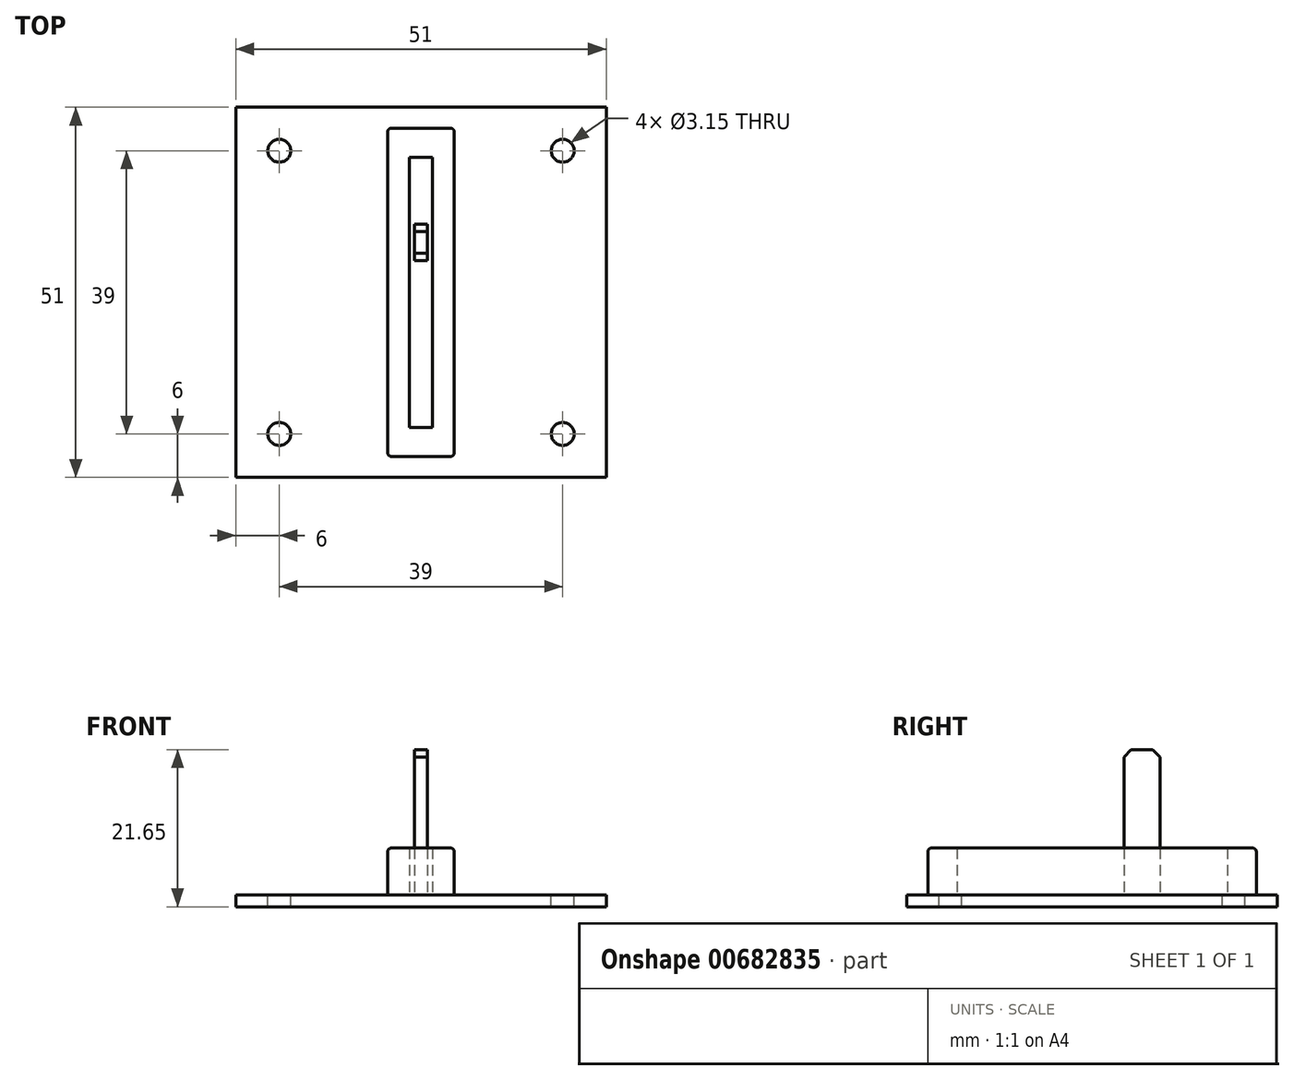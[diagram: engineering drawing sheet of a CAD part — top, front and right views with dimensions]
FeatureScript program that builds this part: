
annotation { "Feature Type Name" : "Feature", "Feature Type Description" : "" }
export const myFeature = defineFeature(function(context is Context, id is Id, definition is map)
    precondition{}
    {
        {
            var Q0;
            Q0=qCreatedBy(makeId("Top.planeOp"),FACE);
            var sketch = newSketch(context, id + "F0", { "sketchPlane" : qUnion([Q0])});
            skLineSegment(sketch, "E0.bottom", {"start": v(-25.5, 25.5) * mm, "end": v(25.5, 25.5) * mm});
            skLineSegment(sketch, "E0.top", {"start": v(-25.5, -25.5) * mm, "end": v(25.5, -25.5) * mm});
            skLineSegment(sketch, "E0.left", {"start": v(-25.5, 25.5) * mm, "end": v(-25.5, -25.5) * mm});
            skLineSegment(sketch, "E0.right", {"start": v(25.5, 25.5) * mm, "end": v(25.5, -25.5) * mm});
            skPoint(sketch, "E1", {"position": v(-19.5, 19.5) * mm});
            skPoint(sketch, "E2.MirrorP", {"position": v(19.5, 19.5) * mm});
            skPoint(sketch, "E3.MirrorP", {"position": v(19.5, -19.5) * mm});
            skPoint(sketch, "E4.MirrorP", {"position": v(-19.5, -19.5) * mm});
            skSolve(sketch);
        }
        {
            var Q0;
            Q0=qCreatedBy(makeId("Top.planeOp"),FACE);
            var sketch = newSketch(context, id + "F1", { "sketchPlane" : qUnion([Q0])});
            skLineSegment(sketch, "E5.bottom", {"start": v(-4.58, 22.6) * mm, "end": v(4.58, 22.6) * mm});
            skLineSegment(sketch, "E5.top", {"start": v(-4.58, -22.6) * mm, "end": v(4.58, -22.6) * mm});
            skLineSegment(sketch, "E5.left", {"start": v(-4.58, 22.6) * mm, "end": v(-4.58, -22.6) * mm});
            skLineSegment(sketch, "E5.right", {"start": v(4.58, 22.6) * mm, "end": v(4.58, -22.6) * mm});
            skLineSegment(sketch, "E6.bottom", {"start": v(-1.58, 18.6) * mm, "end": v(1.58, 18.6) * mm});
            skLineSegment(sketch, "E6.top", {"start": v(-1.58, -18.6) * mm, "end": v(1.58, -18.6) * mm});
            skLineSegment(sketch, "E6.left", {"start": v(-1.58, 18.6) * mm, "end": v(-1.58, -18.6) * mm});
            skLineSegment(sketch, "E6.right", {"start": v(1.58, 18.6) * mm, "end": v(1.58, -18.6) * mm});
            skSolve(sketch);
        }
        {
            var Q0;
            Q0=qCreatedBy(makeId("Top.planeOp"),FACE);
            var sketch = newSketch(context, id + "F2", { "sketchPlane" : qUnion([Q0])});
            skLineSegment(sketch, "E7.bottom", {"start": v(-0.9, 9.37) * mm, "end": v(0.9, 9.37) * mm});
            skLineSegment(sketch, "E7.top", {"start": v(-0.9, 4.37) * mm, "end": v(0.9, 4.37) * mm});
            skLineSegment(sketch, "E7.left", {"start": v(-0.9, 9.37) * mm, "end": v(-0.9, 4.37) * mm});
            skLineSegment(sketch, "E7.right", {"start": v(0.9, 9.37) * mm, "end": v(0.9, 4.37) * mm});
            skSolve(sketch);
        }
        {
            var Q0;
            Q0=makeQuery(id+"F0.imprint","IMPRINT",FACE,{"disambiguationData":[TD([[makeQuery(id+"F0.imprint","IMPRINT",EDGE,{"derivedFrom":sQuery(id+"F0.wireOp",EDGE,"E0.bottom")}),-1.0]])]});
            extrude(context, id + "F3", {"entities" : qUnion([Q0]), "oppositeDirection" : true, "depth" : 1.65 * mm, "offsetDistance" : 25 * mm});
        }
        {
            var Q0;
            Q0=sQuery(id+"F0.wireOp",VERTEX,"E1");
            var Q1;
            Q1=sQuery(id+"F0.wireOp",VERTEX,"E2.MirrorP");
            var Q2;
            Q2=sQuery(id+"F0.wireOp",VERTEX,"E3.MirrorP");
            var Q3;
            Q3=sQuery(id+"F0.wireOp",VERTEX,"E4.MirrorP");
            var Q4;
            Q4=makeQuery(id+"F3.opExtrude","SWEPT_BODY",BODY,{"disambiguationData":[OSD([sQuery(id+"F0.wireOp",EDGE,"E0.bottom"),sQuery(id+"F0.wireOp",EDGE,"E0.top"),sQuery(id+"F0.wireOp",EDGE,"E0.left"),sQuery(id+"F0.wireOp",EDGE,"E0.right")])]});
            hole(context, id + "F4", {"style" : HoleStyle.SIMPLE, "endStyle" : HoleEndStyle.THROUGH, "standardTappedOrClearance" : lookupTablePath({ "standard" : "ISO", "fit" : "Close", "size" : "M3", "type" : "Clearance" }), "standardBlindInLast" : lookupTablePath({ "fit" : "Close", "standard" : "ISO", "size" : "M3", "type" : "Clearance" }), "holeDiameter" : 3.15 * mm, "majorDiameter" : 5 * mm, "isTappedThrough" : true, "tappedDepth" : 12 * mm, "tapClearance" : 3, "locations" : qUnion([Q0, Q1, Q2, Q3]), "scope" : qUnion([Q4])});
        }
        {
            var Q0;
            Q0 = qSketchRegion(id + "F1", true);
            extrude(context, id + "F5", {"entities" : qUnion([Q0]), "operationType" : NewBodyOperationType.ADD, "depth" : 6.45 * mm, "offsetDistance" : 25 * mm});
        }
        {
            var Q0;
            Q0=makeQuery(id+"F5.opExtrude","SWEPT_EDGE",EDGE,{"disambiguationData":[OSD([sQuery(id+"F1.wireOp",EDGE,"E5.bottom"),sQuery(id+"F1.wireOp",EDGE,"E5.right")])]});
            var Q1;
            Q1=makeQuery(id+"F5.opExtrude","SWEPT_EDGE",EDGE,{"disambiguationData":[OSD([sQuery(id+"F1.wireOp",EDGE,"E5.bottom"),sQuery(id+"F1.wireOp",EDGE,"E5.left")])]});
            var Q2;
            Q2=makeQuery(id+"F5.opExtrude","SWEPT_EDGE",EDGE,{"disambiguationData":[OSD([sQuery(id+"F1.wireOp",EDGE,"E5.top"),sQuery(id+"F1.wireOp",EDGE,"E5.right")])]});
            var Q3;
            Q3=makeQuery(id+"F5.opExtrude","SWEPT_EDGE",EDGE,{"disambiguationData":[OSD([sQuery(id+"F1.wireOp",EDGE,"E5.top"),sQuery(id+"F1.wireOp",EDGE,"E5.left")])]});
            var Q4;
            Q4=makeQuery(id+"F5.opExtrude","CAP_EDGE",EDGE,{"disambiguationData":[OSD([sQuery(id+"F1.wireOp",EDGE,"E5.right")])],"isStart":false});
            var Q5;
            Q5=makeQuery(id+"F5.opExtrude","CAP_EDGE",EDGE,{"disambiguationData":[OSD([sQuery(id+"F1.wireOp",EDGE,"E5.left")])],"isStart":false});
            var Q6;
            Q6=makeQuery(id+"F5.opExtrude","CAP_EDGE",EDGE,{"disambiguationData":[OSD([sQuery(id+"F1.wireOp",EDGE,"E5.top")])],"isStart":false});
            var Q7;
            Q7=makeQuery(id+"F5.opExtrude","CAP_EDGE",EDGE,{"disambiguationData":[OSD([sQuery(id+"F1.wireOp",EDGE,"E5.bottom")])],"isStart":false});
            fillet(context, id + "F6", {"entities" : qUnion([Q0, Q1, Q2, Q3, Q4, Q5, Q6, Q7]), "radius" : 0.5 * mm, "tangentPropagation" : true, "allowEdgeOverflow" : false});
        }
        {
            var Q0;
            Q0 = qSketchRegion(id + "F2", true);
            extrude(context, id + "F7", {"entities" : qUnion([Q0]), "operationType" : NewBodyOperationType.ADD, "depth" : 20 * mm, "offsetDistance" : 25 * mm});
        }
        {
            var Q0;
            Q0=makeQuery(id+"F7.opExtrude","CAP_EDGE",EDGE,{"disambiguationData":[OSD([sQuery(id+"F2.wireOp",EDGE,"E7.top")])],"isStart":false});
            var Q1;
            Q1=makeQuery(id+"F7.opExtrude","CAP_EDGE",EDGE,{"disambiguationData":[OSD([sQuery(id+"F2.wireOp",EDGE,"E7.bottom")])],"isStart":false});
            chamfer(context, id + "F8", {"entities" : qUnion([Q0, Q1]), "width" : 1 * mm, "tangentPropagation" : true});
        }
    });
